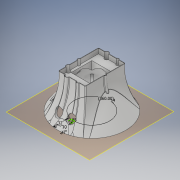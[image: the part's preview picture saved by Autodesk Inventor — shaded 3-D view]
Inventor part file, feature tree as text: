
AUTODESK INVENTOR PART (.ipt)
format: ipt  version: 2019.4 (Build 234330000, 330)  size: 1,244,160 bytes
history: native  units: mm
features: sketch x13, extrude x10, plane x8, hole x8, fillet x3, delete_face x2, revolve x1, loft x1, other x1
ambient origin geometry x8: Origin, YZ Plane, XZ Plane, XY Plane, X Axis, Y Axis, Z Axis, Center Point
bodies: Solid1 (feature_tree)
feature tree (47):
  revolve  "Revolution1"  [1 undecoded]
  extrude  "Extrusion2"  Depth=94.0mm
  plane  "Work Plane1"
  sketch  "Sketch5"  dims[d10=0.0mm d12=180.0deg]
  plane  "Work Plane2"
  plane  "Work Plane6"
  sketch  "Sketch8"  dims[d23=3.0mm d24=170.0mm d25=0.0mm]
  loft  "Loft2"
  extrude  "Extrusion4"  Depth=50.0mm
  delete_face  "Delete Face1"
  delete_face  "Delete Face2"
  sketch  "Sketch10"  dims[d27=90.0mm d28=85.0mm]
  hole  "Hole1"  [1 undecoded]
  hole  "Hole2"  [1 undecoded]
  hole  "Hole3"  [1 undecoded]
  hole  "Hole4"  [1 undecoded]
  hole  "Hole5"  [1 undecoded]
  hole  "Hole6"  [1 undecoded]
  hole  "Hole7"  [1 undecoded]
  hole  "Hole8"  [1 undecoded]
  plane  "Work Plane7"
  extrude  "Extrusion5"  Depth=8.0mm
  fillet  "Fillet4"  Radius=15.0mm
  fillet  "Fillet5"  Radius=17.0mm
  fillet  "Fillet6"  Radius=9.0mm
  plane  "Work Plane8"
  extrude  "Extrusion7"  Depth=17.0mm
  plane  "Work Plane9"
  sketch  "Sketch15"  dims[d45=83.0mm d46=41.5mm]
  extrude  "Extrusion8"  Depth=18.0mm
  extrude  "Extrusion9"  Depth=8.0mm
  extrude  "Extrusion10"  Depth=6.0mm
  extrude  "Extrusion11"  Depth=6.0mm
  plane  "Work Plane10"
  extrude  "Extrusion12"  Depth=6.0mm
  plane  "Work Plane11"
  extrude  "Extrusion13"  Depth=8.0mm
  sketch  "Sketch2"  dims[d3=5.0mm d4=1.5mm]
  sketch  "Sketch4"  dims[d5=80.0mm d8=94.0mm]
  other  "Edges2"
  sketch  "Sketch11"  dims[d29=57.0mm d30=28.5mm]
  sketch  "Sketch13"  dims[d31=42.5mm d32=-10.0mm d37=9.0mm]
  sketch  "Sketch16"  dims[d49=55.0mm d50=27.5mm]
  sketch  "Sketch17"  dims[d51=5.0mm d53=5.0mm]
  sketch  "Sketch18"  dims[d54=5.0mm d55=5.0mm]
  sketch  "Sketch19"  dims[d56=9.0mm d58=8.0mm d59=15.0mm d60=15.0mm d61=17.0mm d62=9.0mm d63=17.0mm d64=18.0mm d65=8.0mm d66=6.0mm d67=6.0mm d68=6.0mm d69=8.0mm d70=9.0mm d71=6.0mm d91=85.0mm d92=57.0mm d93=28.5mm d94=83.0mm d95=55.0mm d96=5.0mm d97=5.0mm d98=5.0mm d99=5.0mm d100=9.0mm d101=8.0mm d102=9.0mm d103=8.0mm d104=6.0mm d105=6.0mm d106=6.0mm d107=8.0mm d108=9.0mm d109=6.0mm d110=0.0mm d111=90.0deg d112=0.0mm d113=90.0deg d114=0.0mm d115=90.0deg d118=10.0mm d119=0.0mm d120=5.0mm d121=0.0mm d122=151.0mm d124=8.0mm d125=6.0mm d126=4.0mm d127=2.0mm d128=90.0deg d129=8.0mm d130=20.594885mm d131=8.0mm d132=6.0mm d133=4.0mm d134=2.0mm d135=90.0deg d136=8.0mm d137=20.594885mm d138=5.0mm d139=6.0mm d140=4.0mm d141=2.0mm d142=90.0deg d143=8.0mm d144=20.594885mm d145=5.0mm d146=6.0mm d147=4.0mm d148=2.0mm d149=90.0deg d150=8.0mm d151=20.594885mm d152=5.0mm d153=6.0mm d154=4.0mm d155=2.0mm d156=90.0deg d157=8.0mm d158=20.594885mm d159=5.0mm d160=6.0mm d161=4.0mm d162=2.0mm d163=90.0deg d164=8.0mm d165=20.594885mm d166=8.0mm d167=6.0mm d168=4.0mm d169=2.0mm d170=90.0deg d171=8.0mm d172=20.594885mm d173=151.0mm d174=30.683mm d175=3.023mm d176=2.0mm d177=14.3117mm d178=0.1mm d179=12.391838mm d180=86.25mm d181=26.0mm d182=13.0mm d183=13.0mm d184=16.0mm d185=16.0mm d186=30.0mm d187=170.0mm d188=0.0mm d189=2.0mm d190=2.0mm d191=2.0mm d192=10.0mm d193=2.85mm d203=10.0mm d204=7.0mm d208=1.0mm d209=32.0mm d210=14.0mm d216=40.0mm d218=360.0deg d220=2.0mm d221=0.0mm d222=46.0mm d236=2.0mm d237=0.0mm d238=5.0mm d239=41.509691mm d240=2.5mm d241=40.0mm d242=10.0mm d243=25.0mm d244=0.0mm d245=17.5mm d246=3.0mm d247=3.0mm d248=3.0mm d249=3.0mm d250=19.0mm d251=24.0mm d252=0.0mm d253=0.0mm d254=44.0mm d255=44.0mm d256=22.0mm d257=22.0mm d258=31.25mm d259=0.0mm d260=-79.5mm d261=12.0mm d262=55.0mm d263=51.5mm d264=0.0mm d265=0.0mm d266=10.0mm d267=0.0mm]
  sketch  "Sketch6"  dims[d15=0.0mm d22=50.0mm]
note: 9 required parameter values undecoded (feature->parameter linkage not recoverable at this tier; creation-order binding heuristic only, values carry confidence <= 0.55)